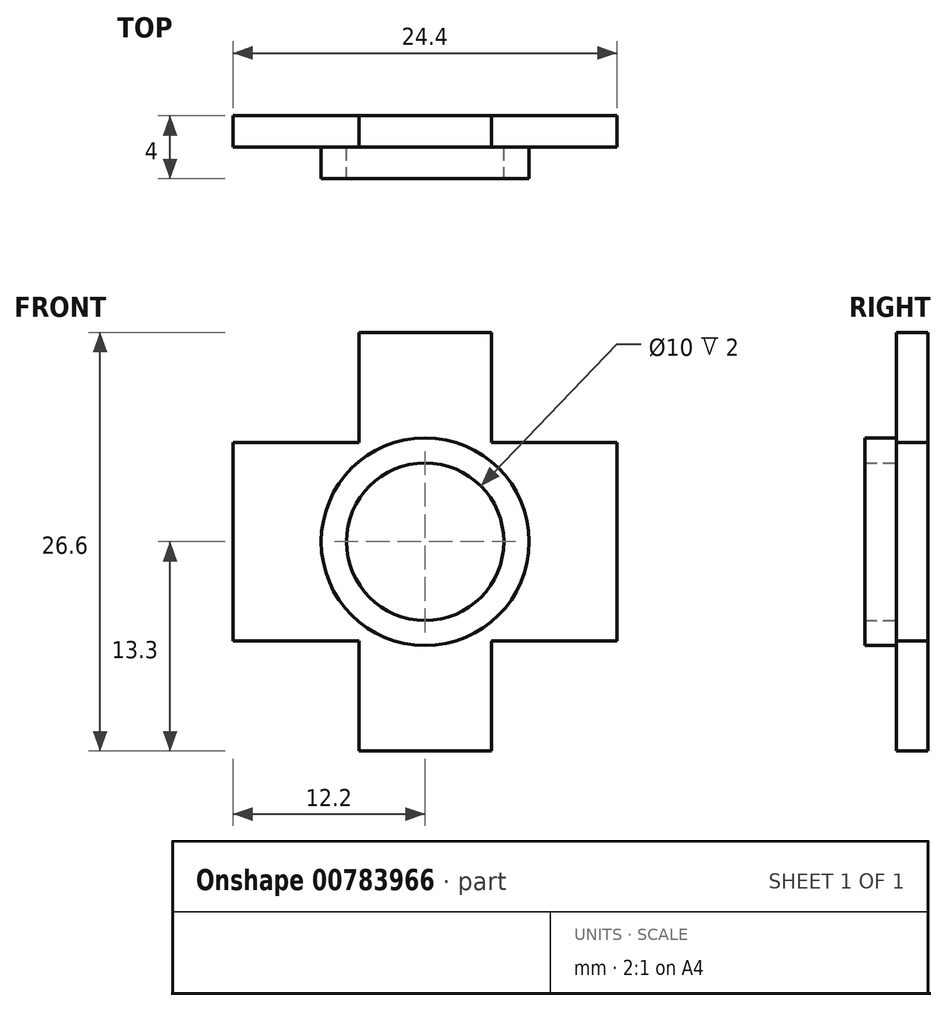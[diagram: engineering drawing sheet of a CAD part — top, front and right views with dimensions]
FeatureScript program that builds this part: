
annotation { "Feature Type Name" : "Feature", "Feature Type Description" : "" }
export const myFeature = defineFeature(function(context is Context, id is Id, definition is map)
    precondition{}
    {
        {
            var Q0;
            Q0=qCreatedBy(makeId("Front.planeOp"),FACE);
            var sketch = newSketch(context, id + "F0", { "sketchPlane" : qUnion([Q0])});
            skLineSegment(sketch, "E0", {"start": v(0, 0) * mm, "end": v(0, 13.3) * mm, "construction": true});
            skLineSegment(sketch, "E1", {"start": v(0, 13.3) * mm, "end": v(-4.2, 13.3) * mm});
            skLineSegment(sketch, "E2", {"start": v(-4.2, 13.3) * mm, "end": v(-4.2, 6.3) * mm});
            skLineSegment(sketch, "E3", {"start": v(-4.2, 6.3) * mm, "end": v(-12.2, 6.3) * mm});
            skLineSegment(sketch, "E4", {"start": v(-12.2, 6.3) * mm, "end": v(-12.2, 0) * mm});
            skLineSegment(sketch, "E5", {"start": v(-12.2, 0) * mm, "end": v(0, 0) * mm, "construction": true});
            skLineSegment(sketch, "E6.MirrorCS", {"start": v(-12.2, -6.3) * mm, "end": v(-12.2, 0) * mm});
            skLineSegment(sketch, "E7.MirrorCS", {"start": v(-4.2, -6.3) * mm, "end": v(-12.2, -6.3) * mm});
            skLineSegment(sketch, "E8.MirrorCS", {"start": v(-4.2, -13.3) * mm, "end": v(-4.2, -6.3) * mm});
            skLineSegment(sketch, "E9.MirrorCS", {"start": v(0, -13.3) * mm, "end": v(-4.2, -13.3) * mm});
            skLineSegment(sketch, "E10.MirrorCS", {"start": v(0, 13.3) * mm, "end": v(4.2, 13.3) * mm});
            skLineSegment(sketch, "E11.MirrorCS", {"start": v(4.2, 13.3) * mm, "end": v(4.2, 6.3) * mm});
            skLineSegment(sketch, "E12.MirrorCS", {"start": v(4.2, 6.3) * mm, "end": v(12.2, 6.3) * mm});
            skLineSegment(sketch, "E13.MirrorCS", {"start": v(12.2, 6.3) * mm, "end": v(12.2, 0) * mm});
            skLineSegment(sketch, "E14.MirrorCS", {"start": v(12.2, -6.3) * mm, "end": v(12.2, 0) * mm});
            skLineSegment(sketch, "E15.MirrorCS", {"start": v(4.2, -6.3) * mm, "end": v(12.2, -6.3) * mm});
            skLineSegment(sketch, "E16.MirrorCS", {"start": v(4.2, -13.3) * mm, "end": v(4.2, -6.3) * mm});
            skLineSegment(sketch, "E17.MirrorCS", {"start": v(0, -13.3) * mm, "end": v(4.2, -13.3) * mm});
            skSolve(sketch);
        }
        {
            var Q0;
            Q0=makeQuery(id+"F0.imprint","IMPRINT",FACE,{"disambiguationData":[TD([[makeQuery(id+"F0.imprint","IMPRINT",EDGE,{"derivedFrom":sQuery(id+"F0.wireOp",EDGE,"E1")}),1.0]])]});
            extrude(context, id + "F1", {"entities" : qUnion([Q0]), "depth" : 2 * mm, "offsetDistance" : 25 * mm});
        }
        {
            var Q0;
            Q0=makeQuery(id+"F1.opExtrude","CAP_FACE",FACE,{"disambiguationData":[OSD([sQuery(id+"F0.wireOp",EDGE,"E1"),sQuery(id+"F0.wireOp",EDGE,"E2"),sQuery(id+"F0.wireOp",EDGE,"E3"),sQuery(id+"F0.wireOp",EDGE,"E4"),sQuery(id+"F0.wireOp",EDGE,"E6.MirrorCS"),sQuery(id+"F0.wireOp",EDGE,"E7.MirrorCS"),sQuery(id+"F0.wireOp",EDGE,"E8.MirrorCS"),sQuery(id+"F0.wireOp",EDGE,"E9.MirrorCS"),sQuery(id+"F0.wireOp",EDGE,"E10.MirrorCS"),sQuery(id+"F0.wireOp",EDGE,"E11.MirrorCS"),sQuery(id+"F0.wireOp",EDGE,"E12.MirrorCS"),sQuery(id+"F0.wireOp",EDGE,"E13.MirrorCS"),sQuery(id+"F0.wireOp",EDGE,"E14.MirrorCS"),sQuery(id+"F0.wireOp",EDGE,"E15.MirrorCS"),sQuery(id+"F0.wireOp",EDGE,"E16.MirrorCS"),sQuery(id+"F0.wireOp",EDGE,"E17.MirrorCS")])],"isStart":false});
            var sketch = newSketch(context, id + "F2", { "sketchPlane" : qUnion([Q0])});
            skCircle(sketch, "E18", {"center": v(0, 0) * mm, "radius": 6.6 * mm});
            skCircle(sketch, "E19", {"center": v(0, 0) * mm, "radius": 5 * mm});
            skSolve(sketch);
        }
        {
            var Q0;
            Q0=makeQuery(id+"F2.imprint","IMPRINT",FACE,{"disambiguationData":[TD([[makeQuery(id+"F2.imprint","IMPRINT",EDGE,{"derivedFrom":sQuery(id+"F2.wireOp",EDGE,"E18")}),1.0]])]});
            extrude(context, id + "F3", {"entities" : qUnion([Q0]), "operationType" : NewBodyOperationType.ADD, "depth" : 2 * mm, "offsetDistance" : 25 * mm});
        }
    });
